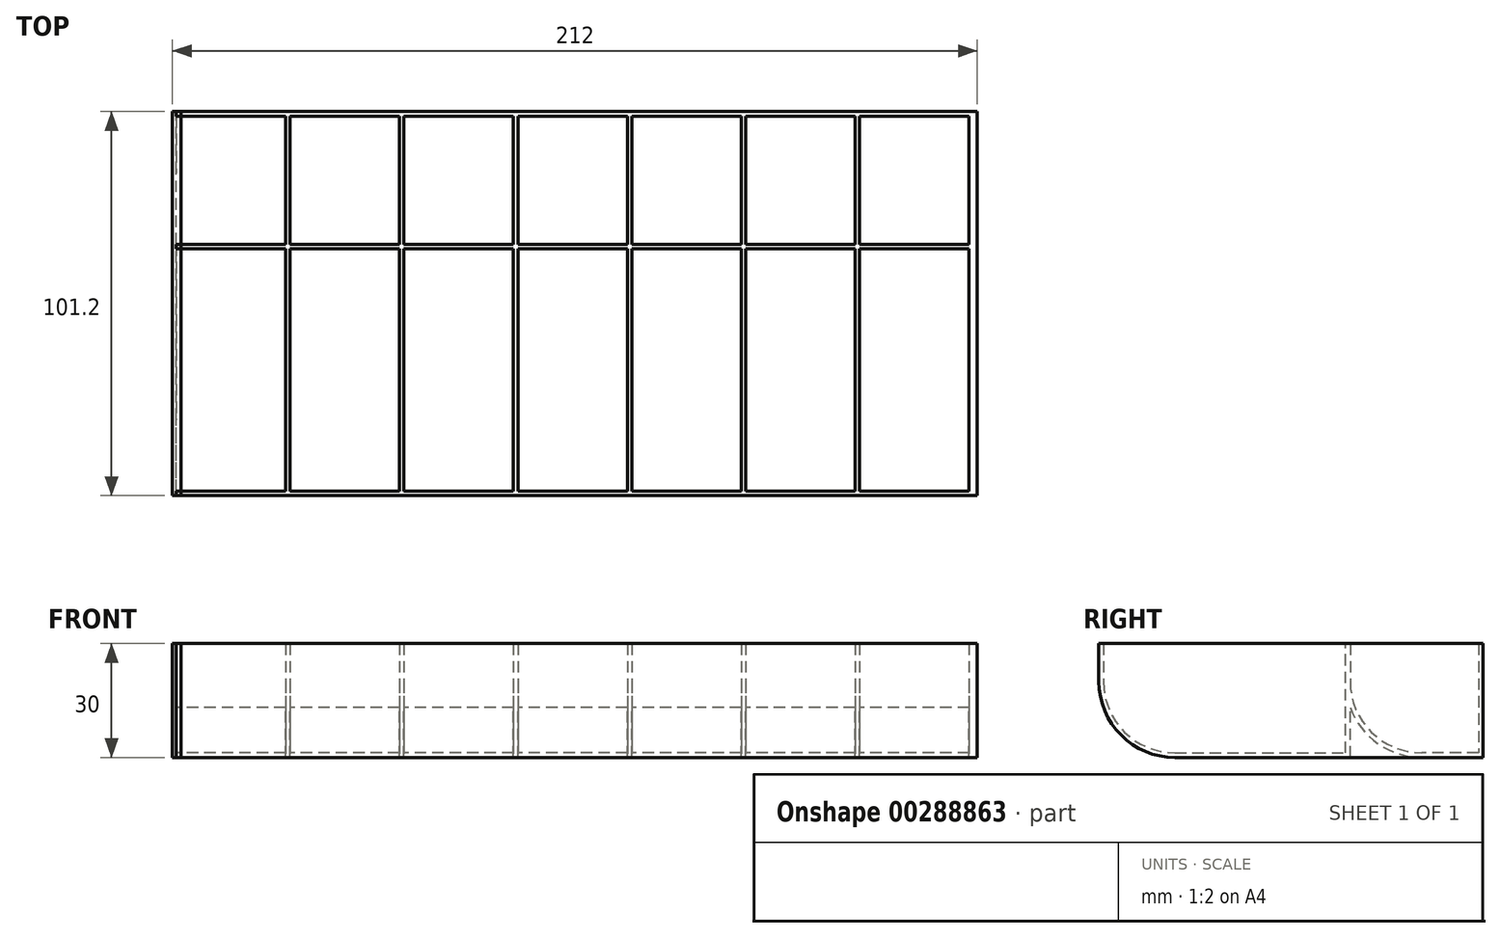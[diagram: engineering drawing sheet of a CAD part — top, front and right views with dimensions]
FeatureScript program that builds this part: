
annotation { "Feature Type Name" : "Feature", "Feature Type Description" : "" }
export const myFeature = defineFeature(function(context is Context, id is Id, definition is map)
    precondition{}
    {
        {
            var Q0;
            Q0=qCreatedBy(makeId("Right.planeOp"),FACE);
            var sketch = newSketch(context, id + "F0", { "sketchPlane" : qUnion([Q0])});
            skLineSegment(sketch, "E0", {"start": v(0, 0) * mm, "end": v(-45, 0) * mm});
            skLineSegment(sketch, "E1", {"start": v(-65, 20) * mm, "end": v(-65, 30) * mm});
            skLineSegment(sketch, "E2", {"start": v(35, 30) * mm, "end": v(35, 0) * mm});
            skLineSegment(sketch, "E3", {"start": v(35, 0) * mm, "end": v(20, 0) * mm});
            skPoint(sketch, "E4.visualSharp", {"position": v(-65, 0) * mm});
            skArc(sketch, "E4.filletArc", {"start": v(-65, 20) * mm, "mid": v(-59.14, 5.86) * mm, "end": v(-45, 0) * mm});
            skLineSegment(sketch, "E5", {"start": v(0, 0) * mm, "end": v(0, 30) * mm});
            skArc(sketch, "E6.filletArc", {"start": v(0, 20) * mm, "mid": v(5.86, 5.86) * mm, "end": v(20, 0) * mm});
            skLineSegment(sketch, "E7", {"start": v(-65, 20) * mm, "end": v(35, 20) * mm, "construction": true});
            skLineSegment(sketch, "E8", {"start": v(-45, 0) * mm, "end": v(-45, 30) * mm, "construction": true});
            skLineSegment(sketch, "E9", {"start": v(20, 0) * mm, "end": v(20, 30) * mm, "construction": true});
            skLineSegment(sketch, "E10", {"start": v(-65, 30) * mm, "end": v(-63.8, 30) * mm});
            skLineSegment(sketch, "E11", {"start": v(-63.8, 30) * mm, "end": v(-63.8, 20) * mm});
            skLineSegment(sketch, "E12", {"start": v(0, 30) * mm, "end": v(1.2, 30) * mm});
            skLineSegment(sketch, "E13", {"start": v(1.2, 30) * mm, "end": v(1.2, 20) * mm});
            skArc(sketch, "E14", {"start": v(-63.8, 20) * mm, "mid": v(-58.3, 6.7) * mm, "end": v(-45, 1.2) * mm});
            skLineSegment(sketch, "E15", {"start": v(-45, 1.2) * mm, "end": v(0, 1.2) * mm});
            skLineSegment(sketch, "E16", {"start": v(35, 0) * mm, "end": v(35, 1.2) * mm});
            skLineSegment(sketch, "E17", {"start": v(35, 1.2) * mm, "end": v(20, 1.2) * mm});
            skArc(sketch, "E18", {"start": v(1.2, 20) * mm, "mid": v(6.7, 6.7) * mm, "end": v(20, 1.2) * mm});
            skLineSegment(sketch, "E19", {"start": v(35, 0) * mm, "end": v(36.2, 0) * mm});
            skLineSegment(sketch, "E20", {"start": v(36.2, 0) * mm, "end": v(36.2, 30) * mm});
            skLineSegment(sketch, "E21", {"start": v(36.2, 30) * mm, "end": v(35, 30) * mm});
            skLineSegment(sketch, "E22", {"start": v(0, 0) * mm, "end": v(1.2, 0) * mm});
            skLineSegment(sketch, "E23", {"start": v(1.2, 0) * mm, "end": v(1.2, 13.18) * mm});
            skLineSegment(sketch, "E24.trimOffspring", {"start": v(1.2, 0) * mm, "end": v(0, 0) * mm});
            skLineSegment(sketch, "E25", {"start": v(-65, 30) * mm, "end": v(36.2, 30) * mm, "construction": true});
            skSolve(sketch);
        }
        {
            var Q0;
            Q0 = qSketchRegion(id + "F0", true);
            extrude(context, id + "F1", {"entities" : qUnion([Q0]), "depth" : 210 * mm});
        }
        {
            var Q0;
            Q0=qCreatedBy(makeId("Right.planeOp"),FACE);
            var sketch = newSketch(context, id + "F2", { "sketchPlane" : qUnion([Q0])});
            skPoint(sketch, "E26.0", {"position": v(-65, 20) * mm});
            skPoint(sketch, "E27.0", {"position": v(-65, 30) * mm});
            skPoint(sketch, "E28.0", {"position": v(-45, 0) * mm});
            skPoint(sketch, "E29.0", {"position": v(36.2, 0) * mm});
            skPoint(sketch, "E30.0", {"position": v(36.2, 30) * mm});
            skLineSegment(sketch, "E31", {"start": v(-65, 20) * mm, "end": v(-65, 30) * mm});
            skLineSegment(sketch, "E32", {"start": v(36.2, 30) * mm, "end": v(36.2, 0) * mm});
            skArc(sketch, "E33", {"start": v(-65, 20) * mm, "mid": v(-59.14, 5.86) * mm, "end": v(-45, 0) * mm});
            skLineSegment(sketch, "E34", {"start": v(-45, 0) * mm, "end": v(36.2, 0) * mm});
            skLineSegment(sketch, "E35", {"start": v(36.2, 30) * mm, "end": v(-65, 30) * mm});
            skSolve(sketch);
        }
        {
            var Q0;
            Q0 = qSketchRegion(id + "F2", true);
            extrude(context, id + "F3", {"entities" : qUnion([Q0]), "depth" : 1.2 * mm, "hasSecondDirection" : true, "secondDirectionOppositeDirection" : true, "secondDirectionDepth" : 1 * mm});
        }
        {
            var Q0;
            Q0 = qSketchRegion(id + "F2", true);
            extrude(context, id + "F4", {"entities" : qUnion([Q0]), "operationType" : NewBodyOperationType.ADD, "depth" : 30 * mm, "hasSecondDirection" : true, "secondDirectionOppositeDirection" : false, "secondDirectionDepth" : 28.8 * mm});
        }
        {
            var Q0;
            Q0 = qSketchRegion(id + "F2", true);
            extrude(context, id + "F5", {"entities" : qUnion([Q0]), "operationType" : NewBodyOperationType.ADD, "depth" : 60 * mm, "hasSecondDirection" : true, "secondDirectionOppositeDirection" : false, "secondDirectionDepth" : 58.8 * mm});
        }
        {
            var Q0;
            Q0 = qSketchRegion(id + "F2", true);
            extrude(context, id + "F6", {"entities" : qUnion([Q0]), "operationType" : NewBodyOperationType.ADD, "depth" : 90 * mm, "hasSecondDirection" : true, "secondDirectionOppositeDirection" : false, "secondDirectionDepth" : 88.8 * mm});
        }
        {
            var Q0;
            Q0 = qSketchRegion(id + "F2", true);
            extrude(context, id + "F7", {"entities" : qUnion([Q0]), "operationType" : NewBodyOperationType.ADD, "depth" : 120 * mm, "hasSecondDirection" : true, "secondDirectionOppositeDirection" : false, "secondDirectionDepth" : 118.8 * mm});
        }
        {
            var Q0;
            Q0 = qSketchRegion(id + "F2", true);
            extrude(context, id + "F8", {"entities" : qUnion([Q0]), "operationType" : NewBodyOperationType.ADD, "depth" : 150 * mm, "hasSecondDirection" : true, "secondDirectionOppositeDirection" : false, "secondDirectionDepth" : 148.8 * mm});
        }
        {
            var Q0;
            Q0 = qSketchRegion(id + "F2", true);
            extrude(context, id + "F9", {"entities" : qUnion([Q0]), "operationType" : NewBodyOperationType.ADD, "depth" : 180 * mm, "hasSecondDirection" : true, "secondDirectionOppositeDirection" : false, "secondDirectionDepth" : 178.8 * mm});
        }
        {
            var Q0;
            Q0 = qSketchRegion(id + "F2", true);
            extrude(context, id + "F10", {"entities" : qUnion([Q0]), "operationType" : NewBodyOperationType.ADD, "depth" : 211 * mm, "hasSecondDirection" : true, "secondDirectionOppositeDirection" : false, "secondDirectionDepth" : 208.8 * mm});
        }
    });
